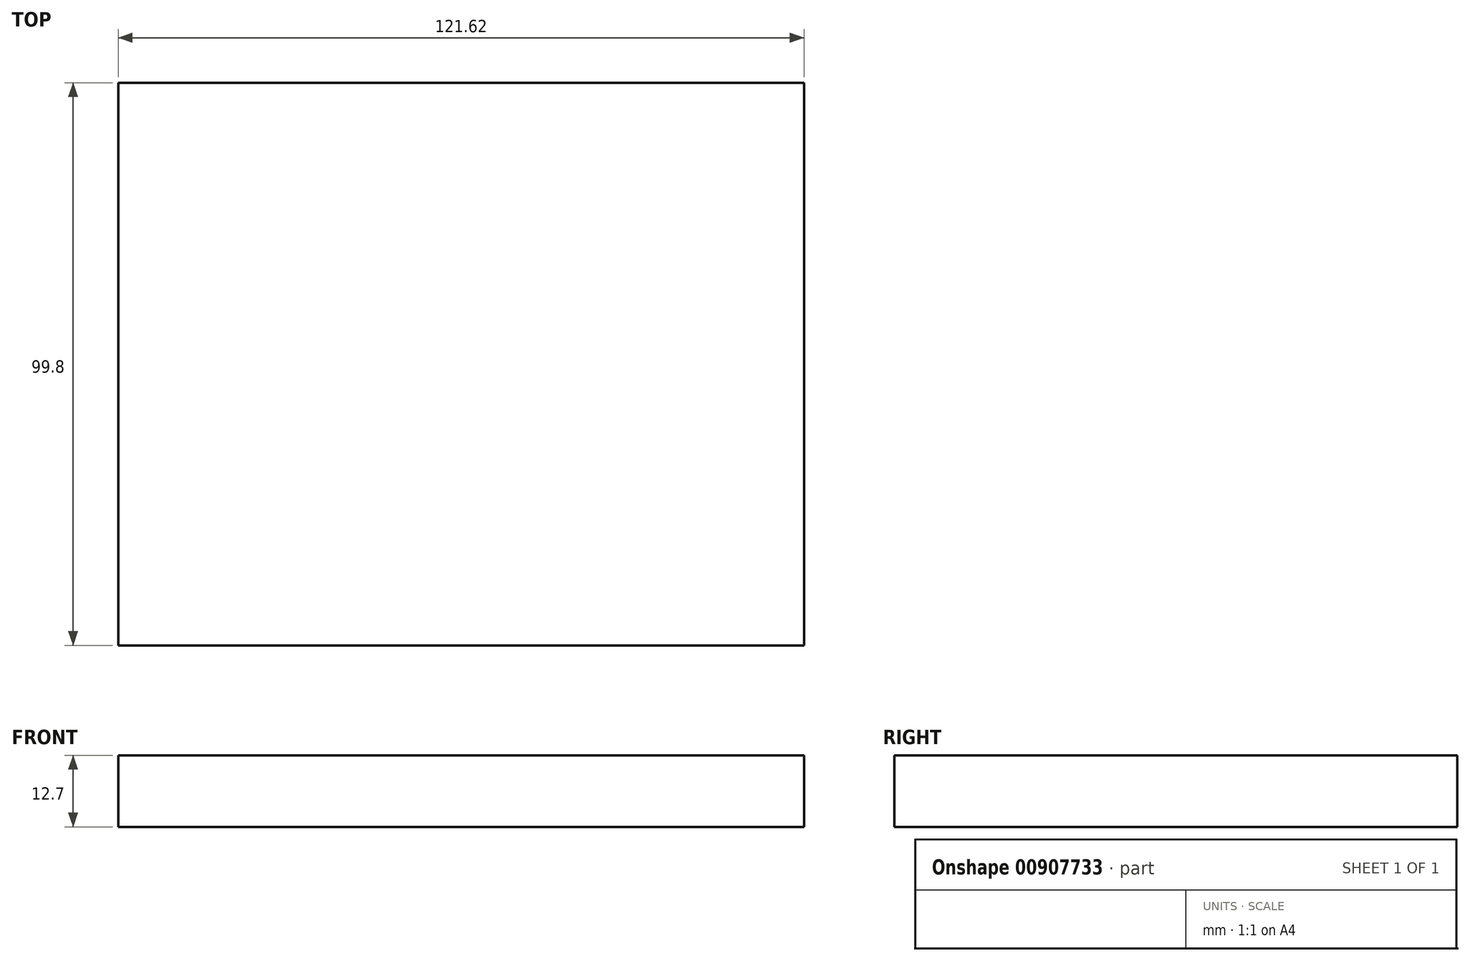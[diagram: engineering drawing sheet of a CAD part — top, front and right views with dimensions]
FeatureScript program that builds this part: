
annotation { "Feature Type Name" : "Feature", "Feature Type Description" : "" }
export const myFeature = defineFeature(function(context is Context, id is Id, definition is map)
    precondition{}
    {
        {
            var Q0;
            Q0=qCreatedBy(makeId("Top.planeOp"),FACE);
            var sketch = newSketch(context, id + "F0", { "sketchPlane" : qUnion([Q0])});
            skLineSegment(sketch, "E0.bottom", {"start": v(-61.88, -47.96) * mm, "end": v(59.74, -47.96) * mm});
            skLineSegment(sketch, "E0.top", {"start": v(-61.88, 51.84) * mm, "end": v(59.74, 51.84) * mm});
            skLineSegment(sketch, "E0.left", {"start": v(-61.88, -47.96) * mm, "end": v(-61.88, 51.84) * mm});
            skLineSegment(sketch, "E0.right", {"start": v(59.74, -47.96) * mm, "end": v(59.74, 51.84) * mm});
            skSolve(sketch);
        }
        {
            var Q0;
            Q0=makeQuery(id+"F0.imprint","IMPRINT",FACE,{"disambiguationData":[TD([[makeQuery(id+"F0.imprint","IMPRINT",EDGE,{"derivedFrom":sQuery(id+"F0.wireOp",EDGE,"E0.bottom")}),1.0]])]});
            extrude(context, id + "F1", {"entities" : qUnion([Q0]), "endBound" : BoundingType.SYMMETRIC, "depth" : 12.7 * mm, "offsetDistance" : 25.4 * mm});
        }
    });
